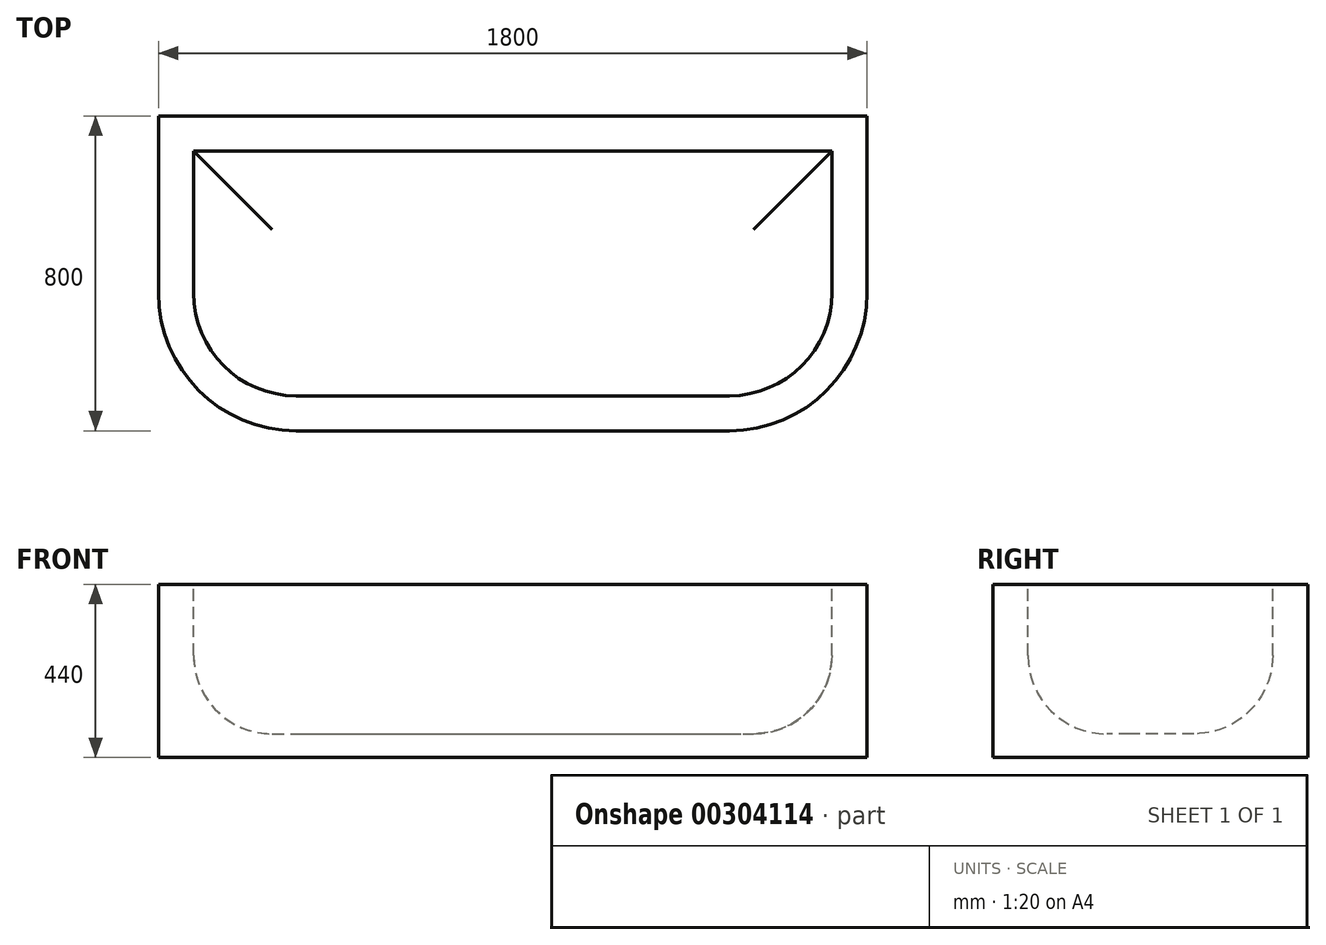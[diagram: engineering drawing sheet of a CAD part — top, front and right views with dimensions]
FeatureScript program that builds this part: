
annotation { "Feature Type Name" : "Feature", "Feature Type Description" : "" }
export const myFeature = defineFeature(function(context is Context, id is Id, definition is map)
    precondition{}
    {
        {
            var Q0;
            Q0=qCreatedBy(makeId("Top.planeOp"),FACE);
            var sketch = newSketch(context, id + "F0", { "sketchPlane" : qUnion([Q0])});
            skLineSegment(sketch, "E0.bottom", {"start": v(-901.62, 214.86) * mm, "end": v(898.38, 214.86) * mm});
            skLineSegment(sketch, "E0.top", {"start": v(-901.62, -585.14) * mm, "end": v(898.38, -585.14) * mm});
            skLineSegment(sketch, "E0.left", {"start": v(-901.62, 214.86) * mm, "end": v(-901.62, -585.14) * mm});
            skLineSegment(sketch, "E0.right", {"start": v(898.38, 214.86) * mm, "end": v(898.38, -585.14) * mm});
            skSolve(sketch);
        }
        {
            var Q0;
            Q0=makeQuery(id+"F0.imprint","IMPRINT",FACE,{"disambiguationData":[TD([[makeQuery(id+"F0.imprint","IMPRINT",EDGE,{"derivedFrom":sQuery(id+"F0.wireOp",EDGE,"E0.bottom")}),-1.0]])]});
            extrude(context, id + "F1", {"entities" : qUnion([Q0]), "depth" : 440 * mm, "offsetDistance" : 25 * mm});
        }
        {
            var Q0;
            Q0=makeQuery(id+"F1.opExtrude","SWEPT_EDGE",EDGE,{"disambiguationData":[OSD([sQuery(id+"F0.wireOp",EDGE,"E0.top"),sQuery(id+"F0.wireOp",EDGE,"E0.left")])]});
            var Q1;
            Q1=makeQuery(id+"F1.opExtrude","SWEPT_EDGE",EDGE,{"disambiguationData":[OSD([sQuery(id+"F0.wireOp",EDGE,"E0.top"),sQuery(id+"F0.wireOp",EDGE,"E0.right")])]});
            fillet(context, id + "F2", {"entities" : qUnion([Q0, Q1]), "radius" : 350 * mm, "tangentPropagation" : true, "allowEdgeOverflow" : false});
        }
        {
            var Q0;
            Q0=makeQuery(id+"F1.opExtrude","CAP_FACE",FACE,{"disambiguationData":[OSD([sQuery(id+"F0.wireOp",EDGE,"E0.bottom"),sQuery(id+"F0.wireOp",EDGE,"E0.top"),sQuery(id+"F0.wireOp",EDGE,"E0.left"),sQuery(id+"F0.wireOp",EDGE,"E0.right")])],"isStart":false});
            var sketch = newSketch(context, id + "F3", { "sketchPlane" : qUnion([Q0])});
            skLineSegment(sketch, "E1.0", {"start": v(-812.62, 125.86) * mm, "end": v(809.38, 125.86) * mm});
            skArc(sketch, "E1.1", {"start": v(-812.62, -235.14) * mm, "mid": v(-736.18, -419.7) * mm, "end": v(-551.62, -496.14) * mm});
            skLineSegment(sketch, "E1.2", {"start": v(-551.62, -496.14) * mm, "end": v(548.38, -496.14) * mm});
            skLineSegment(sketch, "E1.3", {"start": v(-812.62, 125.86) * mm, "end": v(-812.62, -235.14) * mm});
            skArc(sketch, "E1.4", {"start": v(548.38, -496.14) * mm, "mid": v(732.93, -419.7) * mm, "end": v(809.38, -235.14) * mm});
            skLineSegment(sketch, "E1.5", {"start": v(809.38, 125.86) * mm, "end": v(809.38, -235.14) * mm});
            skSolve(sketch);
        }
        {
            var Q0;
            Q0=makeQuery(id+"F3.imprint","IMPRINT",FACE,{"disambiguationData":[TD([[makeQuery(id+"F3.imprint","IMPRINT",EDGE,{"derivedFrom":sQuery(id+"F3.wireOp",EDGE,"E1.0")}),-1.0]])]});
            extrude(context, id + "F4", {"entities" : qUnion([Q0]), "operationType" : NewBodyOperationType.REMOVE, "oppositeDirection" : true, "depth" : 380 * mm, "offsetDistance" : 25 * mm});
        }
        {
            var Q0;
            Q0=makeQuery(id+"F4.boolean.opBoolean","COPY",EDGE,{"derivedFrom":makeQuery(id+"F4.opExtrude","CAP_EDGE",EDGE,{"disambiguationData":[OSD([sQuery(id+"F3.wireOp",EDGE,"E1.3")])],"isStart":false})});
            var Q1;
            Q1=makeQuery(id+"F4.boolean.opBoolean","COPY",EDGE,{"derivedFrom":makeQuery(id+"F4.opExtrude","CAP_EDGE",EDGE,{"disambiguationData":[OSD([sQuery(id+"F3.wireOp",EDGE,"E1.1")])],"isStart":false})});
            var Q2;
            Q2=makeQuery(id+"F4.boolean.opBoolean","COPY",EDGE,{"derivedFrom":makeQuery(id+"F4.opExtrude","CAP_EDGE",EDGE,{"disambiguationData":[OSD([sQuery(id+"F3.wireOp",EDGE,"E1.0")])],"isStart":false})});
            var Q3;
            Q3=makeQuery(id+"F4.boolean.opBoolean","COPY",EDGE,{"derivedFrom":makeQuery(id+"F4.opExtrude","CAP_EDGE",EDGE,{"disambiguationData":[OSD([sQuery(id+"F3.wireOp",EDGE,"E1.5")])],"isStart":false})});
            var Q4;
            Q4=makeQuery(id+"F4.boolean.opBoolean","COPY",EDGE,{"derivedFrom":makeQuery(id+"F4.opExtrude","CAP_EDGE",EDGE,{"disambiguationData":[OSD([sQuery(id+"F3.wireOp",EDGE,"E1.4")])],"isStart":false})});
            var Q5;
            Q5=makeQuery(id+"F4.boolean.opBoolean","COPY",EDGE,{"derivedFrom":makeQuery(id+"F4.opExtrude","CAP_EDGE",EDGE,{"disambiguationData":[OSD([sQuery(id+"F3.wireOp",EDGE,"E1.2")])],"isStart":false})});
            fillet(context, id + "F5", {"entities" : qUnion([Q0, Q1, Q2, Q3, Q4, Q5]), "radius" : 200 * mm, "tangentPropagation" : true, "allowEdgeOverflow" : false});
        }
    });
